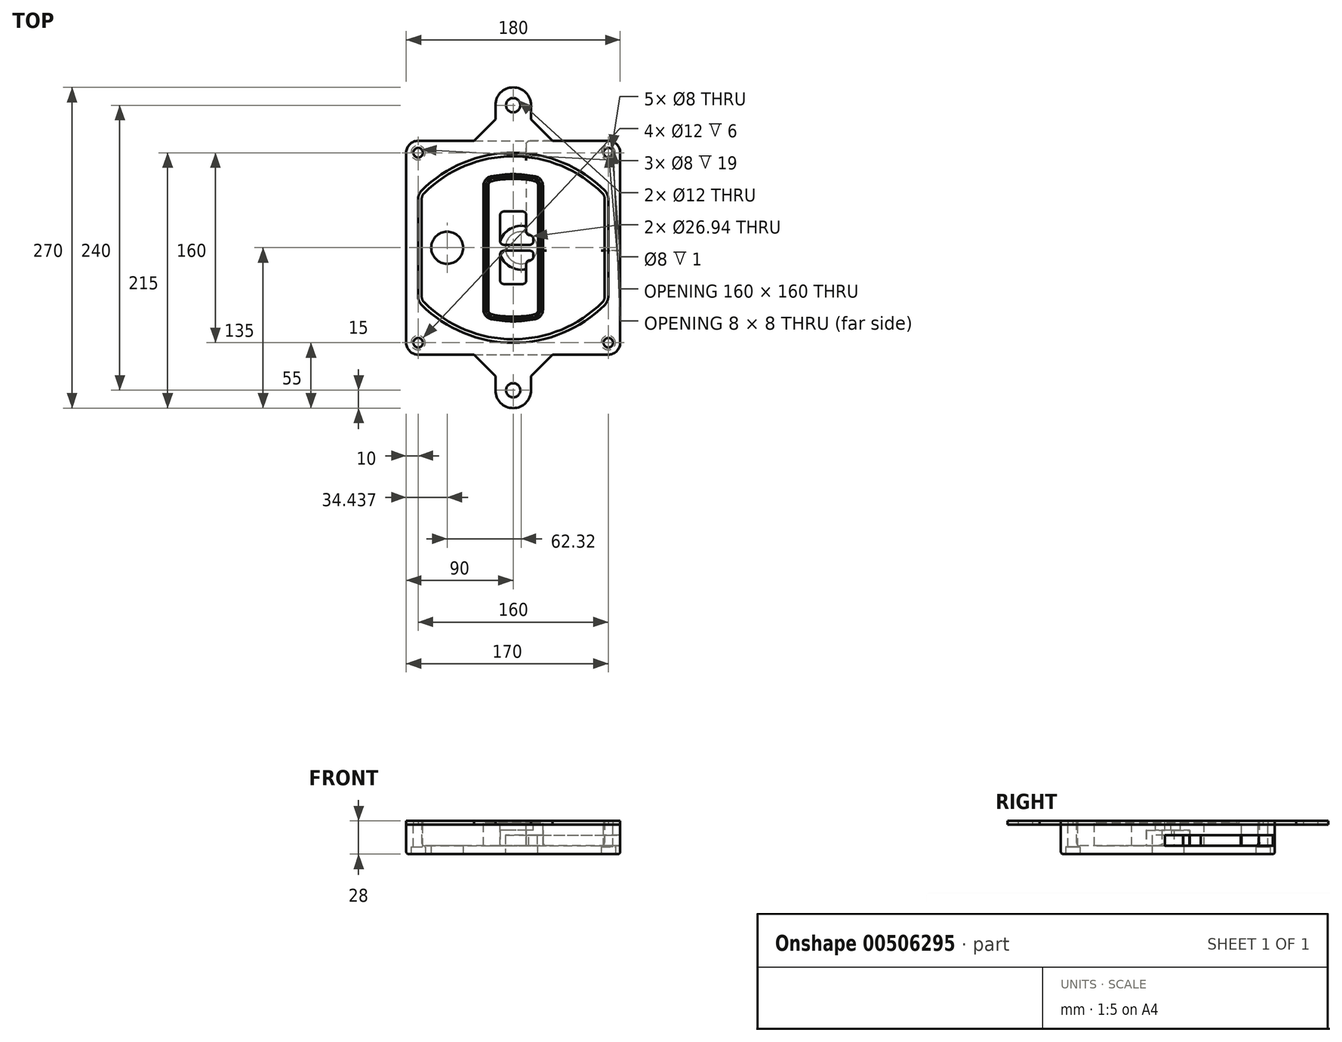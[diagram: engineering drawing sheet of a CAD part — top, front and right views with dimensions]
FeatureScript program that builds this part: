
annotation { "Feature Type Name" : "Feature", "Feature Type Description" : "" }
export const myFeature = defineFeature(function(context is Context, id is Id, definition is map)
    precondition{}
    {
        {
            var Q0;
            Q0=qCreatedBy(makeId("Top.planeOp"),FACE);
            var sketch = newSketch(context, id + "F0", { "sketchPlane" : qUnion([Q0])});
            skPoint(sketch, "E0.rect.middle", {"position": v(0, 0) * mm});
            skLineSegment(sketch, "E1.bottom", {"start": v(-80, -90) * mm, "end": v(80, -90) * mm});
            skLineSegment(sketch, "E1.top", {"start": v(-80, 90) * mm, "end": v(80, 90) * mm});
            skLineSegment(sketch, "E1.left", {"start": v(-90, -80) * mm, "end": v(-90, 80) * mm});
            skLineSegment(sketch, "E1.right", {"start": v(90, -80) * mm, "end": v(90, 80) * mm});
            skLineSegment(sketch, "E2", {"start": v(-90, 90) * mm, "end": v(90, -90) * mm, "construction": true});
            skLineSegment(sketch, "E3", {"start": v(90, 90) * mm, "end": v(-90, -90) * mm, "construction": true});
            skCircle(sketch, "E4", {"center": v(-80, 80) * mm, "radius": 4 * mm});
            skCircle(sketch, "E5", {"center": v(80, 80) * mm, "radius": 4 * mm});
            skCircle(sketch, "E6", {"center": v(80, -80) * mm, "radius": 4 * mm});
            skCircle(sketch, "E7", {"center": v(-80, -80) * mm, "radius": 4 * mm});
            skLineSegment(sketch, "E8", {"start": v(-80, 80) * mm, "end": v(80, 80) * mm, "construction": true});
            skLineSegment(sketch, "E9", {"start": v(80, 80) * mm, "end": v(80, -80) * mm, "construction": true});
            skLineSegment(sketch, "E10", {"start": v(80, -80) * mm, "end": v(-80, -80) * mm, "construction": true});
            skLineSegment(sketch, "E11", {"start": v(-80, -80) * mm, "end": v(-80, 80) * mm, "construction": true});
            skLineSegment(sketch, "E12", {"start": v(-80, 40.98) * mm, "end": v(-80, -40.98) * mm});
            skLineSegment(sketch, "E13", {"start": v(80, 40.98) * mm, "end": v(80, -40.98) * mm});
            skArc(sketch, "E14", {"start": v(77.08, 48.04) * mm, "mid": v(0, 80) * mm, "end": v(-77.08, 48.04) * mm});
            skArc(sketch, "E15", {"start": v(-77.08, -48.04) * mm, "mid": v(0, -80) * mm, "end": v(77.08, -48.04) * mm});
            skLineSegment(sketch, "E16", {"start": v(-80, 0) * mm, "end": v(80, 0) * mm, "construction": true});
            skPoint(sketch, "E17.visualSharp", {"position": v(-80, -45) * mm});
            skArc(sketch, "E17.filletArc", {"start": v(-80, -40.98) * mm, "mid": v(-79.24, -44.8) * mm, "end": v(-77.08, -48.04) * mm});
            skPoint(sketch, "E18.visualSharp", {"position": v(-80, 45) * mm});
            skArc(sketch, "E18.filletArc", {"start": v(-77.08, 48.04) * mm, "mid": v(-79.24, 44.8) * mm, "end": v(-80, 40.98) * mm});
            skPoint(sketch, "E19.visualSharp", {"position": v(80, 45) * mm});
            skArc(sketch, "E19.filletArc", {"start": v(80, 40.98) * mm, "mid": v(79.24, 44.8) * mm, "end": v(77.08, 48.04) * mm});
            skPoint(sketch, "E20.visualSharp", {"position": v(80, -45) * mm});
            skArc(sketch, "E20.filletArc", {"start": v(77.08, -48.04) * mm, "mid": v(79.24, -44.8) * mm, "end": v(80, -40.98) * mm});
            skPoint(sketch, "E21.visualSharp", {"position": v(-90, 90) * mm});
            skArc(sketch, "E21.filletArc", {"start": v(-80, 90) * mm, "mid": v(-87.07, 87.07) * mm, "end": v(-90, 80) * mm});
            skPoint(sketch, "E22.visualSharp", {"position": v(90, 90) * mm});
            skArc(sketch, "E22.filletArc", {"start": v(90, 80) * mm, "mid": v(87.07, 87.07) * mm, "end": v(80, 90) * mm});
            skPoint(sketch, "E23.visualSharp", {"position": v(90, -90) * mm});
            skArc(sketch, "E23.filletArc", {"start": v(80, -90) * mm, "mid": v(87.07, -87.07) * mm, "end": v(90, -80) * mm});
            skPoint(sketch, "E24.visualSharp", {"position": v(-90, -90) * mm});
            skArc(sketch, "E24.filletArc", {"start": v(-90, -80) * mm, "mid": v(-87.07, -87.07) * mm, "end": v(-80, -90) * mm});
            skArc(sketch, "E25.0", {"start": v(77, 40.98) * mm, "mid": v(76.47, 43.65) * mm, "end": v(74.95, 45.92) * mm});
            skLineSegment(sketch, "E25.1", {"start": v(77, 40.98) * mm, "end": v(77, -40.98) * mm});
            skArc(sketch, "E25.2", {"start": v(74.95, -45.92) * mm, "mid": v(76.47, -43.65) * mm, "end": v(77, -40.98) * mm});
            skArc(sketch, "E25.3", {"start": v(-74.95, -45.92) * mm, "mid": v(0, -77) * mm, "end": v(74.95, -45.92) * mm});
            skArc(sketch, "E25.4", {"start": v(-77, -40.98) * mm, "mid": v(-76.47, -43.65) * mm, "end": v(-74.95, -45.92) * mm});
            skArc(sketch, "E25.5", {"start": v(74.95, 45.92) * mm, "mid": v(0, 77) * mm, "end": v(-74.95, 45.92) * mm});
            skLineSegment(sketch, "E25.6", {"start": v(-77, 40.98) * mm, "end": v(-77, -40.98) * mm});
            skArc(sketch, "E25.7", {"start": v(-74.95, 45.92) * mm, "mid": v(-76.47, 43.65) * mm, "end": v(-77, 40.98) * mm});
            skArc(sketch, "E26.0", {"start": v(-79.9, 50.87) * mm, "mid": v(-82.94, 46.33) * mm, "end": v(-84, 40.98) * mm});
            skArc(sketch, "E26.1", {"start": v(79.9, 50.87) * mm, "mid": v(0, 84) * mm, "end": v(-79.9, 50.87) * mm});
            skArc(sketch, "E26.2", {"start": v(84, 40.98) * mm, "mid": v(82.94, 46.33) * mm, "end": v(79.9, 50.87) * mm});
            skLineSegment(sketch, "E26.3", {"start": v(84, 40.98) * mm, "end": v(84, -40.98) * mm});
            skArc(sketch, "E26.4", {"start": v(79.9, -50.87) * mm, "mid": v(82.94, -46.33) * mm, "end": v(84, -40.98) * mm});
            skLineSegment(sketch, "E26.5", {"start": v(-84, 40.98) * mm, "end": v(-84, -40.98) * mm});
            skArc(sketch, "E26.6", {"start": v(-79.9, -50.87) * mm, "mid": v(0, -84) * mm, "end": v(79.9, -50.87) * mm});
            skArc(sketch, "E26.7", {"start": v(-84, -40.98) * mm, "mid": v(-82.94, -46.33) * mm, "end": v(-79.9, -50.87) * mm});
            skSolve(sketch);
        }
        {
            var Q0;
            Q0=makeQuery(id+"F0.imprint","IMPRINT",FACE,{"disambiguationData":[TD([[makeQuery(id+"F0.imprint","IMPRINT",EDGE,{"derivedFrom":sQuery(id+"F0.wireOp",EDGE,"E1.bottom")}),1.0]])]});
            var Q1;
            Q1=makeQuery(id+"F0.imprint","IMPRINT",FACE,{"disambiguationData":[TD([[makeQuery(id+"F0.imprint","IMPRINT",EDGE,{"derivedFrom":sQuery(id+"F0.wireOp",EDGE,"E12")}),1.0]])]});
            var Q2;
            Q2=makeQuery(id+"F0.imprint","IMPRINT",FACE,{"disambiguationData":[TD([[makeQuery(id+"F0.imprint","IMPRINT",EDGE,{"derivedFrom":sQuery(id+"F0.wireOp",EDGE,"E25.0")}),1.0]])]});
            var Q3;
            Q3=makeQuery(id+"F0.imprint","IMPRINT",FACE,{"disambiguationData":[TD([[makeQuery(id+"F0.imprint","IMPRINT",EDGE,{"derivedFrom":sQuery(id+"F0.wireOp",EDGE,"E12")}),-1.0]])]});
            extrude(context, id + "F1", {"entities" : qUnion([Q0, Q1, Q2, Q3]), "oppositeDirection" : true, "depth" : 25 * mm});
        }
        {
            var Q0;
            Q0=makeQuery(id+"F0.imprint","IMPRINT",FACE,{"disambiguationData":[TD([[makeQuery(id+"F0.imprint","IMPRINT",EDGE,{"derivedFrom":sQuery(id+"F0.wireOp",EDGE,"E12")}),1.0]])]});
            extrude(context, id + "F2", {"entities" : qUnion([Q0]), "operationType" : NewBodyOperationType.ADD, "depth" : 3 * mm});
        }
        {
            var Q0;
            Q0=makeQuery(id+"F0.imprint","IMPRINT",FACE,{"disambiguationData":[TD([[makeQuery(id+"F0.imprint","IMPRINT",EDGE,{"derivedFrom":sQuery(id+"F0.wireOp",EDGE,"E25.0")}),1.0]])]});
            extrude(context, id + "F3", {"entities" : qUnion([Q0]), "operationType" : NewBodyOperationType.REMOVE, "oppositeDirection" : true, "depth" : 18 * mm});
        }
        {
            var Q0;
            Q0=makeQuery(id+"F2.opExtrude","CAP_FACE",FACE,{"disambiguationData":[OSD([sQuery(id+"F0.wireOp",EDGE,"E12"),sQuery(id+"F0.wireOp",EDGE,"E13"),sQuery(id+"F0.wireOp",EDGE,"E14"),sQuery(id+"F0.wireOp",EDGE,"E15"),sQuery(id+"F0.wireOp",EDGE,"E17.filletArc"),sQuery(id+"F0.wireOp",EDGE,"E18.filletArc"),sQuery(id+"F0.wireOp",EDGE,"E19.filletArc"),sQuery(id+"F0.wireOp",EDGE,"E20.filletArc"),sQuery(id+"F0.wireOp",EDGE,"E25.0"),sQuery(id+"F0.wireOp",EDGE,"E25.1"),sQuery(id+"F0.wireOp",EDGE,"E25.2"),sQuery(id+"F0.wireOp",EDGE,"E25.3"),sQuery(id+"F0.wireOp",EDGE,"E25.4"),sQuery(id+"F0.wireOp",EDGE,"E25.5"),sQuery(id+"F0.wireOp",EDGE,"E25.6"),sQuery(id+"F0.wireOp",EDGE,"E25.7")])],"isStart":false});
            var sketch = newSketch(context, id + "F4", { "sketchPlane" : qUnion([Q0])});
            skArc(sketch, "E27.0", {"start": v(-18.64, -60.07) * mm, "mid": v(0, -62) * mm, "end": v(18.64, -60.07) * mm});
            skArc(sketch, "E28.0", {"start": v(18.64, 60.07) * mm, "mid": v(0, 62) * mm, "end": v(-18.64, 60.07) * mm});
            skLineSegment(sketch, "E29", {"start": v(-25, 52.24) * mm, "end": v(-25, -52.24) * mm});
            skLineSegment(sketch, "E30", {"start": v(25, 52.24) * mm, "end": v(25, -52.24) * mm});
            skLineSegment(sketch, "E31", {"start": v(-25, 58.5) * mm, "end": v(25, 58.5) * mm, "construction": true});
            skLineSegment(sketch, "E32", {"start": v(-25, -58.5) * mm, "end": v(25, -58.5) * mm, "construction": true});
            skPoint(sketch, "E33.visualSharp", {"position": v(-25, 58.5) * mm});
            skArc(sketch, "E33.filletArc", {"start": v(-18.64, 60.07) * mm, "mid": v(-23.2, 57.28) * mm, "end": v(-25, 52.24) * mm});
            skPoint(sketch, "E34.visualSharp", {"position": v(25, 58.5) * mm});
            skArc(sketch, "E34.filletArc", {"start": v(25, 52.24) * mm, "mid": v(23.2, 57.28) * mm, "end": v(18.64, 60.07) * mm});
            skPoint(sketch, "E35.visualSharp", {"position": v(25, -58.5) * mm});
            skArc(sketch, "E35.filletArc", {"start": v(18.64, -60.07) * mm, "mid": v(23.2, -57.28) * mm, "end": v(25, -52.24) * mm});
            skPoint(sketch, "E36.visualSharp", {"position": v(-25, -58.5) * mm});
            skArc(sketch, "E36.filletArc", {"start": v(-25, -52.24) * mm, "mid": v(-23.2, -57.28) * mm, "end": v(-18.64, -60.07) * mm});
            skArc(sketch, "E37.0", {"start": v(74.95, 45.92) * mm, "mid": v(0, 77) * mm, "end": v(-74.95, 45.92) * mm});
            skArc(sketch, "E37.1", {"start": v(-74.95, 45.92) * mm, "mid": v(-76.47, 43.65) * mm, "end": v(-77, 40.98) * mm});
            skLineSegment(sketch, "E37.2", {"start": v(-77, 40.98) * mm, "end": v(-77, -40.98) * mm});
            skArc(sketch, "E37.3", {"start": v(-77, -40.98) * mm, "mid": v(-76.47, -43.65) * mm, "end": v(-74.95, -45.92) * mm});
            skArc(sketch, "E37.4", {"start": v(-74.95, -45.92) * mm, "mid": v(0, -77) * mm, "end": v(74.95, -45.92) * mm});
            skArc(sketch, "E37.5", {"start": v(74.95, -45.92) * mm, "mid": v(76.47, -43.65) * mm, "end": v(77, -40.98) * mm});
            skLineSegment(sketch, "E37.6", {"start": v(77, 40.98) * mm, "end": v(77, -40.98) * mm});
            skArc(sketch, "E37.7", {"start": v(77, 40.98) * mm, "mid": v(76.47, 43.65) * mm, "end": v(74.95, 45.92) * mm});
            skLineSegment(sketch, "E38.0", {"start": v(23, 52.24) * mm, "end": v(23, -52.24) * mm});
            skArc(sketch, "E38.1", {"start": v(18.23, -58.11) * mm, "mid": v(21.66, -56.02) * mm, "end": v(23, -52.24) * mm});
            skArc(sketch, "E38.2", {"start": v(-18.23, -58.11) * mm, "mid": v(0, -60) * mm, "end": v(18.23, -58.11) * mm});
            skArc(sketch, "E38.3", {"start": v(-23, -52.24) * mm, "mid": v(-21.66, -56.02) * mm, "end": v(-18.23, -58.11) * mm});
            skLineSegment(sketch, "E38.4", {"start": v(-23, 52.24) * mm, "end": v(-23, -52.24) * mm});
            skArc(sketch, "E38.5", {"start": v(23, 52.24) * mm, "mid": v(21.66, 56.02) * mm, "end": v(18.23, 58.11) * mm});
            skArc(sketch, "E38.6", {"start": v(-18.23, 58.11) * mm, "mid": v(-21.66, 56.02) * mm, "end": v(-23, 52.24) * mm});
            skArc(sketch, "E38.7", {"start": v(18.23, 58.11) * mm, "mid": v(0, 60) * mm, "end": v(-18.23, 58.11) * mm});
            skArc(sketch, "E39.0", {"start": v(21, 52.24) * mm, "mid": v(20.1, 54.76) * mm, "end": v(17.82, 56.15) * mm});
            skLineSegment(sketch, "E39.1", {"start": v(21, 52.24) * mm, "end": v(21, -52.24) * mm});
            skArc(sketch, "E39.2", {"start": v(17.82, -56.15) * mm, "mid": v(20.1, -54.76) * mm, "end": v(21, -52.24) * mm});
            skArc(sketch, "E39.3", {"start": v(-17.82, -56.15) * mm, "mid": v(0, -58) * mm, "end": v(17.82, -56.15) * mm});
            skArc(sketch, "E39.4", {"start": v(-21, -52.24) * mm, "mid": v(-20.1, -54.76) * mm, "end": v(-17.82, -56.15) * mm});
            skArc(sketch, "E39.5", {"start": v(17.82, 56.15) * mm, "mid": v(0, 58) * mm, "end": v(-17.82, 56.15) * mm});
            skLineSegment(sketch, "E39.6", {"start": v(-21, 52.24) * mm, "end": v(-21, -52.24) * mm});
            skArc(sketch, "E39.7", {"start": v(-17.82, 56.15) * mm, "mid": v(-20.1, 54.76) * mm, "end": v(-21, 52.24) * mm});
            skLineSegment(sketch, "E40", {"start": v(-25, 0) * mm, "end": v(25, 0) * mm, "construction": true});
            skLineSegment(sketch, "E41", {"start": v(-11, 5.5) * mm, "end": v(-11, 27.5) * mm});
            skLineSegment(sketch, "E42", {"start": v(-8, 30.5) * mm, "end": v(8, 30.5) * mm});
            skLineSegment(sketch, "E43", {"start": v(11, 27.5) * mm, "end": v(11, 13.5) * mm});
            skLineSegment(sketch, "E44", {"start": v(14, 10.5) * mm, "end": v(14, 10.5) * mm});
            skLineSegment(sketch, "E45", {"start": v(17, 7.5) * mm, "end": v(17, 5.5) * mm});
            skLineSegment(sketch, "E46", {"start": v(14, 2.5) * mm, "end": v(-8, 2.5) * mm});
            skPoint(sketch, "E47.visualSharp", {"position": v(-11, 30.5) * mm});
            skArc(sketch, "E47.filletArc", {"start": v(-8, 30.5) * mm, "mid": v(-10.12, 29.62) * mm, "end": v(-11, 27.5) * mm});
            skPoint(sketch, "E48.visualSharp", {"position": v(11, 30.5) * mm});
            skArc(sketch, "E48.filletArc", {"start": v(11, 27.5) * mm, "mid": v(10.12, 29.62) * mm, "end": v(8, 30.5) * mm});
            skPoint(sketch, "E49.visualSharp", {"position": v(11, 10.5) * mm});
            skArc(sketch, "E49.filletArc", {"start": v(11, 13.5) * mm, "mid": v(11.88, 11.38) * mm, "end": v(14, 10.5) * mm});
            skPoint(sketch, "E50.visualSharp", {"position": v(17, 10.5) * mm});
            skArc(sketch, "E50.filletArc", {"start": v(17, 7.5) * mm, "mid": v(16.12, 9.62) * mm, "end": v(14, 10.5) * mm});
            skPoint(sketch, "E51.visualSharp", {"position": v(17, 2.5) * mm});
            skArc(sketch, "E51.filletArc", {"start": v(14, 2.5) * mm, "mid": v(16.12, 3.38) * mm, "end": v(17, 5.5) * mm});
            skPoint(sketch, "E52.visualSharp", {"position": v(-11, 2.5) * mm});
            skArc(sketch, "E52.filletArc", {"start": v(-11, 5.5) * mm, "mid": v(-10.12, 3.38) * mm, "end": v(-8, 2.5) * mm});
            skLineSegment(sketch, "E53.0.MirrorCS", {"start": v(14, -2.5) * mm, "end": v(-8, -2.5) * mm});
            skArc(sketch, "E54.0.MirrorCS", {"start": v(-11, -5.5) * mm, "mid": v(-10.12, -3.38) * mm, "end": v(-8, -2.5) * mm});
            skLineSegment(sketch, "E55.0.MirrorCS", {"start": v(-11, -5.5) * mm, "end": v(-11, -27.5) * mm});
            skArc(sketch, "E56.0.MirrorCS", {"start": v(-8, -30.5) * mm, "mid": v(-10.12, -29.62) * mm, "end": v(-11, -27.5) * mm});
            skLineSegment(sketch, "E57.0.MirrorCS", {"start": v(-8, -30.5) * mm, "end": v(8, -30.5) * mm});
            skArc(sketch, "E58.0.MirrorCS", {"start": v(11, -27.5) * mm, "mid": v(10.12, -29.62) * mm, "end": v(8, -30.5) * mm});
            skLineSegment(sketch, "E59.0.MirrorCS", {"start": v(11, -27.5) * mm, "end": v(11, -13.5) * mm});
            skArc(sketch, "E60.0.MirrorCS", {"start": v(11, -13.5) * mm, "mid": v(11.88, -11.38) * mm, "end": v(14, -10.5) * mm});
            skArc(sketch, "E61.0.MirrorCS", {"start": v(17, -7.5) * mm, "mid": v(16.12, -9.62) * mm, "end": v(14, -10.5) * mm});
            skLineSegment(sketch, "E62.0.MirrorCS", {"start": v(17, -7.5) * mm, "end": v(17, -5.5) * mm});
            skArc(sketch, "E63.0.MirrorCS", {"start": v(14, -2.5) * mm, "mid": v(16.12, -3.38) * mm, "end": v(17, -5.5) * mm});
            skSolve(sketch);
        }
        {
            var Q0;
            Q0=makeQuery(id+"F4.imprint","IMPRINT",FACE,{"disambiguationData":[TD([[makeQuery(id+"F4.imprint","IMPRINT",EDGE,{"derivedFrom":sQuery(id+"F4.wireOp",EDGE,"E27.0")}),1.0]])]});
            var Q1;
            Q1=makeQuery(id+"F4.imprint","IMPRINT",FACE,{"disambiguationData":[TD([[makeQuery(id+"F4.imprint","IMPRINT",EDGE,{"derivedFrom":sQuery(id+"F4.wireOp",EDGE,"E38.0")}),-1.0]])]});
            var Q2;
            Q2=makeQuery(id+"F4.imprint","IMPRINT",FACE,{"disambiguationData":[TD([[makeQuery(id+"F4.imprint","IMPRINT",EDGE,{"derivedFrom":sQuery(id+"F4.wireOp",EDGE,"E39.0")}),1.0]])]});
            extrude(context, id + "F5", {"entities" : qUnion([Q0, Q1, Q2]), "operationType" : NewBodyOperationType.ADD, "endBound" : BoundingType.UP_TO_NEXT, "oppositeDirection" : true, "depth" : 25 * mm});
        }
        {
            var Q0;
            Q0=makeQuery(id+"F4.imprint","IMPRINT",FACE,{"disambiguationData":[TD([[makeQuery(id+"F4.imprint","IMPRINT",EDGE,{"derivedFrom":sQuery(id+"F4.wireOp",EDGE,"E38.0")}),-1.0]])]});
            extrude(context, id + "F6", {"entities" : qUnion([Q0]), "operationType" : NewBodyOperationType.REMOVE, "oppositeDirection" : true, "depth" : 2 * mm});
        }
        {
            var Q0;
            Q0=makeQuery(id+"F1.opExtrude","CAP_FACE",FACE,{"disambiguationData":[OSD([sQuery(id+"F0.wireOp",EDGE,"E1.bottom"),sQuery(id+"F0.wireOp",EDGE,"E1.top"),sQuery(id+"F0.wireOp",EDGE,"E1.left"),sQuery(id+"F0.wireOp",EDGE,"E1.right"),sQuery(id+"F0.wireOp",EDGE,"E4"),sQuery(id+"F0.wireOp",EDGE,"E5"),sQuery(id+"F0.wireOp",EDGE,"E6"),sQuery(id+"F0.wireOp",EDGE,"E7"),sQuery(id+"F0.wireOp",EDGE,"E21.filletArc"),sQuery(id+"F0.wireOp",EDGE,"E22.filletArc"),sQuery(id+"F0.wireOp",EDGE,"E23.filletArc"),sQuery(id+"F0.wireOp",EDGE,"E24.filletArc")])],"isStart":false});
            var sketch = newSketch(context, id + "F7", { "sketchPlane" : qUnion([Q0])});
            skCircle(sketch, "E64", {"center": v(6.76, 0) * mm, "radius": 13.47 * mm});
            skCircle(sketch, "E65", {"center": v(-55.56, 0) * mm, "radius": 13.47 * mm});
            skLineSegment(sketch, "E66", {"start": v(90, 0) * mm, "end": v(-90, 0) * mm});
            skCircle(sketch, "E67", {"center": v(6.76, 0) * mm, "radius": 18.47 * mm});
            skCircle(sketch, "E68", {"center": v(80, -80) * mm, "radius": 6 * mm});
            skCircle(sketch, "E69", {"center": v(-80, -80) * mm, "radius": 6 * mm});
            skCircle(sketch, "E70", {"center": v(-80, 80) * mm, "radius": 6 * mm});
            skCircle(sketch, "E71", {"center": v(80, 80) * mm, "radius": 6 * mm});
            skSolve(sketch);
        }
        {
            var Q0;
            {var subQ1=sQuery(id+"F7.wireOp",EDGE,"E66");var subQ4=sQuery(id+"F7.wireOp",EDGE,"E64");var subQ6=makeQuery(id+"F7.imprint","INTERSECT",VERTEX,{"disambiguationData":[OD(0.0)],"derivedFrom":[subQ4,subQ1]});Q0=makeQuery(id+"F7.imprint","IMPRINT",FACE,{"disambiguationData":[TD([[makeQuery(id+"F7.imprint","IMPRINT",EDGE,{"disambiguationData":[TD([[subQ6,-1.0]])],"derivedFrom":subQ4}),-1.0]])]});}
            var Q1;
            {var subQ0=sQuery(id+"F7.wireOp",EDGE,"E66");var subQ1=sQuery(id+"F7.wireOp",EDGE,"E64");var subQ3=makeQuery(id+"F7.imprint","INTERSECT",VERTEX,{"disambiguationData":[OD(0.0)],"derivedFrom":[subQ1,subQ0]});Q1=makeQuery(id+"F7.imprint","IMPRINT",FACE,{"disambiguationData":[TD([[makeQuery(id+"F7.imprint","IMPRINT",EDGE,{"disambiguationData":[TD([[subQ3,-1.0]])],"derivedFrom":subQ1}),1.0]])]});}
            var Q2;
            {var subQ0=sQuery(id+"F7.wireOp",EDGE,"E66");var subQ1=sQuery(id+"F7.wireOp",EDGE,"E64");var subQ3=makeQuery(id+"F7.imprint","INTERSECT",VERTEX,{"disambiguationData":[OD(0.0)],"derivedFrom":[subQ1,subQ0]});Q2=makeQuery(id+"F7.imprint","IMPRINT",FACE,{"disambiguationData":[TD([[makeQuery(id+"F7.imprint","IMPRINT",EDGE,{"disambiguationData":[TD([[subQ3,1.0]])],"derivedFrom":subQ1}),1.0]])]});}
            var Q3;
            {var subQ1=sQuery(id+"F7.wireOp",EDGE,"E66");var subQ4=sQuery(id+"F7.wireOp",EDGE,"E64");var subQ6=makeQuery(id+"F7.imprint","INTERSECT",VERTEX,{"disambiguationData":[OD(0.0)],"derivedFrom":[subQ4,subQ1]});Q3=makeQuery(id+"F7.imprint","IMPRINT",FACE,{"disambiguationData":[TD([[makeQuery(id+"F7.imprint","IMPRINT",EDGE,{"disambiguationData":[TD([[subQ6,1.0]])],"derivedFrom":subQ4}),-1.0]])]});}
            extrude(context, id + "F8", {"entities" : qUnion([Q0, Q1, Q2, Q3]), "operationType" : NewBodyOperationType.ADD, "oppositeDirection" : true, "depth" : 20 * mm});
        }
        {
            var Q0;
            {var subQ0=sQuery(id+"F7.wireOp",EDGE,"E66");var subQ1=sQuery(id+"F7.wireOp",EDGE,"E64");var subQ3=makeQuery(id+"F7.imprint","INTERSECT",VERTEX,{"disambiguationData":[OD(0.0)],"derivedFrom":[subQ1,subQ0]});Q0=makeQuery(id+"F7.imprint","IMPRINT",FACE,{"disambiguationData":[TD([[makeQuery(id+"F7.imprint","IMPRINT",EDGE,{"disambiguationData":[TD([[subQ3,-1.0]])],"derivedFrom":subQ1}),1.0]])]});}
            var Q1;
            {var subQ0=sQuery(id+"F7.wireOp",EDGE,"E66");var subQ1=sQuery(id+"F7.wireOp",EDGE,"E64");var subQ3=makeQuery(id+"F7.imprint","INTERSECT",VERTEX,{"disambiguationData":[OD(0.0)],"derivedFrom":[subQ1,subQ0]});Q1=makeQuery(id+"F7.imprint","IMPRINT",FACE,{"disambiguationData":[TD([[makeQuery(id+"F7.imprint","IMPRINT",EDGE,{"disambiguationData":[TD([[subQ3,1.0]])],"derivedFrom":subQ1}),1.0]])]});}
            extrude(context, id + "F9", {"entities" : qUnion([Q0, Q1]), "operationType" : NewBodyOperationType.REMOVE, "oppositeDirection" : true, "depth" : 16 * mm});
        }
        {
            var Q0;
            {var subQ0=sQuery(id+"F7.wireOp",EDGE,"E66");var subQ1=sQuery(id+"F7.wireOp",EDGE,"E65");var subQ3=makeQuery(id+"F7.imprint","INTERSECT",VERTEX,{"disambiguationData":[OD(0.0)],"derivedFrom":[subQ1,subQ0]});Q0=makeQuery(id+"F7.imprint","IMPRINT",FACE,{"disambiguationData":[TD([[makeQuery(id+"F7.imprint","IMPRINT",EDGE,{"disambiguationData":[TD([[subQ3,-1.0]])],"derivedFrom":subQ1}),1.0]])]});}
            var Q1;
            {var subQ0=sQuery(id+"F7.wireOp",EDGE,"E66");var subQ1=sQuery(id+"F7.wireOp",EDGE,"E65");var subQ3=makeQuery(id+"F7.imprint","INTERSECT",VERTEX,{"disambiguationData":[OD(0.0)],"derivedFrom":[subQ1,subQ0]});Q1=makeQuery(id+"F7.imprint","IMPRINT",FACE,{"disambiguationData":[TD([[makeQuery(id+"F7.imprint","IMPRINT",EDGE,{"disambiguationData":[TD([[subQ3,1.0]])],"derivedFrom":subQ1}),1.0]])]});}
            extrude(context, id + "F10", {"entities" : qUnion([Q0, Q1]), "operationType" : NewBodyOperationType.REMOVE, "oppositeDirection" : true, "depth" : 25 * mm});
        }
        {
            var Q0;
            Q0=makeQuery(id+"F7.imprint","IMPRINT",FACE,{"disambiguationData":[TD([[makeQuery(id+"F7.imprint","IMPRINT",EDGE,{"derivedFrom":sQuery(id+"F7.wireOp",EDGE,"E68")}),1.0]])]});
            var Q1;
            Q1=makeQuery(id+"F7.imprint","IMPRINT",FACE,{"disambiguationData":[TD([[makeQuery(id+"F7.imprint","IMPRINT",EDGE,{"derivedFrom":makeQuery(id+"F1.opExtrude","CAP_EDGE",EDGE,{"disambiguationData":[OSD([sQuery(id+"F0.wireOp",EDGE,"E5")])],"isStart":false})}),-1.0]])]});
            var Q2;
            Q2=makeQuery(id+"F7.imprint","IMPRINT",FACE,{"disambiguationData":[TD([[makeQuery(id+"F7.imprint","IMPRINT",EDGE,{"derivedFrom":sQuery(id+"F7.wireOp",EDGE,"E69")}),1.0]])]});
            var Q3;
            Q3=makeQuery(id+"F7.imprint","IMPRINT",FACE,{"disambiguationData":[TD([[makeQuery(id+"F7.imprint","IMPRINT",EDGE,{"derivedFrom":makeQuery(id+"F1.opExtrude","CAP_EDGE",EDGE,{"disambiguationData":[OSD([sQuery(id+"F0.wireOp",EDGE,"E4")])],"isStart":false})}),-1.0]])]});
            var Q4;
            Q4=makeQuery(id+"F7.imprint","IMPRINT",FACE,{"disambiguationData":[TD([[makeQuery(id+"F7.imprint","IMPRINT",EDGE,{"derivedFrom":sQuery(id+"F7.wireOp",EDGE,"E70")}),1.0]])]});
            var Q5;
            Q5=makeQuery(id+"F7.imprint","IMPRINT",FACE,{"disambiguationData":[TD([[makeQuery(id+"F7.imprint","IMPRINT",EDGE,{"derivedFrom":makeQuery(id+"F1.opExtrude","CAP_EDGE",EDGE,{"disambiguationData":[OSD([sQuery(id+"F0.wireOp",EDGE,"E7")])],"isStart":false})}),-1.0]])]});
            var Q6;
            Q6=makeQuery(id+"F7.imprint","IMPRINT",FACE,{"disambiguationData":[TD([[makeQuery(id+"F7.imprint","IMPRINT",EDGE,{"derivedFrom":sQuery(id+"F7.wireOp",EDGE,"E71")}),1.0]])]});
            var Q7;
            Q7=makeQuery(id+"F7.imprint","IMPRINT",FACE,{"disambiguationData":[TD([[makeQuery(id+"F7.imprint","IMPRINT",EDGE,{"derivedFrom":makeQuery(id+"F1.opExtrude","CAP_EDGE",EDGE,{"disambiguationData":[OSD([sQuery(id+"F0.wireOp",EDGE,"E6")])],"isStart":false})}),-1.0]])]});
            extrude(context, id + "F11", {"entities" : qUnion([Q0, Q1, Q2, Q3, Q4, Q5, Q6, Q7]), "operationType" : NewBodyOperationType.REMOVE, "oppositeDirection" : true, "depth" : 6 * mm});
        }
        {
            var Q0;
            Q0=makeQuery(id+"F9.boolean.opBoolean","COPY",FACE,{"derivedFrom":makeQuery(id+"F9.opExtrude","CAP_FACE",FACE,{"disambiguationData":[OSD([sQuery(id+"F7.wireOp",EDGE,"E64")])],"isStart":false})});
            var sketch = newSketch(context, id + "F12", { "sketchPlane" : qUnion([Q0])});
            skArc(sketch, "E72.0", {"start": v(11, -88.19) * mm, "mid": v(97.1, -83.6) * mm, "end": v(92.5, 2.5) * mm});
            skLineSegment(sketch, "E72.1", {"start": v(11, -17.97) * mm, "end": v(11, -17.97) * mm});
            skLineSegment(sketch, "E73", {"start": v(92.5, -105.13) * mm, "end": v(102.3, -105.13) * mm});
            skLineSegment(sketch, "E74.0", {"start": v(92.5, 2.5) * mm, "end": v(14, 2.5) * mm});
            skArc(sketch, "E74.1", {"start": v(14, 2.5) * mm, "mid": v(16.12, 3.38) * mm, "end": v(17, 5.5) * mm});
            skLineSegment(sketch, "E74.2", {"start": v(17, 7.5) * mm, "end": v(17, 5.5) * mm});
            skArc(sketch, "E74.3", {"start": v(17, 7.5) * mm, "mid": v(16.12, 9.62) * mm, "end": v(14, 10.5) * mm});
            skArc(sketch, "E74.4", {"start": v(11, 13.5) * mm, "mid": v(11.88, 11.38) * mm, "end": v(14, 10.5) * mm});
            skLineSegment(sketch, "E74.5", {"start": v(11, 13.5) * mm, "end": v(11, -88.19) * mm});
            skLineSegment(sketch, "E74.7", {"start": v(92.5, -2.5) * mm, "end": v(14, -2.5) * mm});
            skArc(sketch, "E74.8", {"start": v(14, -2.5) * mm, "mid": v(16.12, -3.38) * mm, "end": v(17, -5.5) * mm});
            skLineSegment(sketch, "E74.9", {"start": v(17, -7.5) * mm, "end": v(17, -5.5) * mm});
            skArc(sketch, "E74.10", {"start": v(17, -7.5) * mm, "mid": v(16.12, -9.62) * mm, "end": v(14, -10.5) * mm});
            skArc(sketch, "E74.11", {"start": v(11, -13.5) * mm, "mid": v(11.88, -11.38) * mm, "end": v(14, -10.5) * mm});
            skLineSegment(sketch, "E74.12", {"start": v(11, -17.97) * mm, "end": v(11, -13.5) * mm});
            skPoint(sketch, "E75.orphan", {"position": v(11, -27.5) * mm});
            skPoint(sketch, "E76.orphan", {"position": v(-8, -2.5) * mm});
            skPoint(sketch, "E77.orphan", {"position": v(-8, 2.5) * mm});
            skPoint(sketch, "E78.orphan", {"position": v(11, 27.5) * mm});
            skSolve(sketch);
        }
        {
            var Q0;
            {var subQ7=sQuery(id+"F12.wireOp",EDGE,"E72.0");var subQ14=sQuery(id+"F12.wireOp",EDGE,"E72.1");var subQ16=sQuery(id+"F12.wireOp",EDGE,"E74.1");var subQ18=sQuery(id+"F12.wireOp",EDGE,"E74.8");Q0=qUnion([makeQuery(id+"F12.imprint","IMPRINT",FACE,{"disambiguationData":[TD([[makeQuery(id+"F12.imprint","IMPRINT",EDGE,{"derivedFrom":subQ7}),1.0]])]}),makeQuery(id+"F12.imprint","IMPRINT",FACE,{"disambiguationData":[TD([[makeQuery(id+"F12.imprint","IMPRINT",EDGE,{"derivedFrom":subQ14}),1.0]])]}),makeQuery(id+"F12.imprint","IMPRINT",FACE,{"disambiguationData":[TD([[makeQuery(id+"F12.imprint","IMPRINT",EDGE,{"derivedFrom":subQ16}),1.0]])]}),makeQuery(id+"F12.imprint","IMPRINT",FACE,{"disambiguationData":[TD([[makeQuery(id+"F12.imprint","IMPRINT",EDGE,{"derivedFrom":subQ18}),-1.0]])]})]);}
            var Q1;
            Q1=makeQuery(id+"F5.boolean.opBoolean","SPLIT",FACE,{"disambiguationData":[TD([makeQuery(id+"F5.opExtrude","SWEPT_FACE",FACE,{"disambiguationData":[OSD([sQuery(id+"F4.wireOp",EDGE,"E41")])]})])],"derivedFrom":makeQuery(id+"F3.boolean.opBoolean","COPY",FACE,{"derivedFrom":makeQuery(id+"F3.opExtrude","CAP_FACE",FACE,{"disambiguationData":[OSD([sQuery(id+"F0.wireOp",EDGE,"E25.0"),sQuery(id+"F0.wireOp",EDGE,"E25.1"),sQuery(id+"F0.wireOp",EDGE,"E25.2"),sQuery(id+"F0.wireOp",EDGE,"E25.3"),sQuery(id+"F0.wireOp",EDGE,"E25.4"),sQuery(id+"F0.wireOp",EDGE,"E25.5"),sQuery(id+"F0.wireOp",EDGE,"E25.6"),sQuery(id+"F0.wireOp",EDGE,"E25.7")])],"isStart":false})})});
            extrude(context, id + "F13", {"entities" : qUnion([Q0]), "operationType" : NewBodyOperationType.REMOVE, "endBound" : BoundingType.UP_TO_SURFACE, "endBoundEntityFace" : qUnion([Q1]), "depth" : 25 * mm});
        }
        {
            var Q0;
            Q0=makeQuery(id+"F3.boolean.opBoolean","COPY",EDGE,{"derivedFrom":makeQuery(id+"F3.opExtrude","CAP_EDGE",EDGE,{"disambiguationData":[OSD([sQuery(id+"F0.wireOp",EDGE,"E25.6")])],"isStart":false})});
            var Q1;
            Q1=makeQuery(id+"F8.boolean.opBoolean","INTERSECT",EDGE,{"derivedFrom":[makeQuery(id+"F5.opExtrude","SWEPT_FACE",FACE,{"disambiguationData":[OSD([sQuery(id+"F4.wireOp",EDGE,"E30")])]}),makeQuery(id+"F8.opExtrude","CAP_FACE",FACE,{"disambiguationData":[OSD([sQuery(id+"F7.wireOp",EDGE,"E67")])],"isStart":false})]});
            var Q2;
            Q2=makeQuery(id+"F8.boolean.opBoolean","INTERSECT",EDGE,{"disambiguationData":[OD(1.0)],"derivedFrom":[makeQuery(id+"F5.opExtrude","SWEPT_FACE",FACE,{"disambiguationData":[OSD([sQuery(id+"F4.wireOp",EDGE,"E30")])]}),makeQuery(id+"F8.opExtrude","SWEPT_FACE",FACE,{"disambiguationData":[OSD([sQuery(id+"F7.wireOp",EDGE,"E67")])]})]});
            var Q3;
            {var subQ0=makeQuery(id+"F3.boolean.opBoolean","COPY",FACE,{"derivedFrom":makeQuery(id+"F3.opExtrude","CAP_FACE",FACE,{"disambiguationData":[OSD([sQuery(id+"F0.wireOp",EDGE,"E25.0"),sQuery(id+"F0.wireOp",EDGE,"E25.1"),sQuery(id+"F0.wireOp",EDGE,"E25.2"),sQuery(id+"F0.wireOp",EDGE,"E25.3"),sQuery(id+"F0.wireOp",EDGE,"E25.4"),sQuery(id+"F0.wireOp",EDGE,"E25.5"),sQuery(id+"F0.wireOp",EDGE,"E25.6"),sQuery(id+"F0.wireOp",EDGE,"E25.7")])],"isStart":false})});var subQ1=sQuery(id+"F4.wireOp",EDGE,"E30");Q3=makeQuery(id+"F8.boolean.opBoolean","SPLIT",EDGE,{"disambiguationData":[TD([makeQuery(id+"F5.opExtrude","SWEPT_FACE",FACE,{"disambiguationData":[OSD([sQuery(id+"F4.wireOp",EDGE,"E35.filletArc")])]})])],"derivedFrom":makeQuery(id+"F5.opExtrude","TWEAK_EDGE",EDGE,{"derivedFrom":[subQ0,makeQuery(id+"F4.imprint","IMPRINT",EDGE,{"derivedFrom":subQ1})]})});}
            var Q4;
            {var subQ0=sQuery(id+"F0.wireOp",EDGE,"E25.0");var subQ1=sQuery(id+"F0.wireOp",EDGE,"E25.1");var subQ2=sQuery(id+"F0.wireOp",EDGE,"E25.2");var subQ3=sQuery(id+"F0.wireOp",EDGE,"E25.3");var subQ4=sQuery(id+"F0.wireOp",EDGE,"E25.4");var subQ5=sQuery(id+"F0.wireOp",EDGE,"E25.5");var subQ6=sQuery(id+"F0.wireOp",EDGE,"E25.6");var subQ7=sQuery(id+"F0.wireOp",EDGE,"E25.7");Q4=makeQuery(id+"F8.boolean.opBoolean","INTERSECT",EDGE,{"derivedFrom":[makeQuery(id+"F5.boolean.opBoolean","SPLIT",FACE,{"disambiguationData":[TD([makeQuery(id+"F2.opExtrude","SWEPT_FACE",FACE,{"disambiguationData":[OSD([subQ0])]})])],"derivedFrom":makeQuery(id+"F3.boolean.opBoolean","COPY",FACE,{"derivedFrom":makeQuery(id+"F3.opExtrude","CAP_FACE",FACE,{"disambiguationData":[OSD([subQ0,subQ1,subQ2,subQ3,subQ4,subQ5,subQ6,subQ7])],"isStart":false})})}),makeQuery(id+"F8.opExtrude","SWEPT_FACE",FACE,{"disambiguationData":[OSD([sQuery(id+"F7.wireOp",EDGE,"E67")])]})]});}
            var Q5;
            Q5=makeQuery(id+"F8.boolean.opBoolean","INTERSECT",EDGE,{"disambiguationData":[OD(0.0)],"derivedFrom":[makeQuery(id+"F5.opExtrude","SWEPT_FACE",FACE,{"disambiguationData":[OSD([sQuery(id+"F4.wireOp",EDGE,"E30")])]}),makeQuery(id+"F8.opExtrude","SWEPT_FACE",FACE,{"disambiguationData":[OSD([sQuery(id+"F7.wireOp",EDGE,"E67")])]})]});
            fillet(context, id + "F14", {"entities" : qUnion([Q0, Q1, Q2, Q3, Q4, Q5]), "radius" : 3 * mm, "tangentPropagation" : true, "allowEdgeOverflow" : false});
        }
        {
            var Q0;
            Q0=makeQuery(id+"F1.opExtrude","CAP_EDGE",EDGE,{"disambiguationData":[OSD([sQuery(id+"F0.wireOp",EDGE,"E1.bottom")])],"isStart":false});
            fillet(context, id + "F15", {"entities" : qUnion([Q0]), "radius" : 2 * mm, "tangentPropagation" : true, "allowEdgeOverflow" : false});
        }
        {
            var Q0;
            {var subQ0=sQuery(id+"F0.wireOp",EDGE,"E21.filletArc");var subQ1=sQuery(id+"F0.wireOp",EDGE,"E7");var subQ2=sQuery(id+"F0.wireOp",EDGE,"E6");var subQ3=sQuery(id+"F0.wireOp",EDGE,"E5");var subQ4=sQuery(id+"F0.wireOp",EDGE,"E4");var subQ5=sQuery(id+"F0.wireOp",EDGE,"E22.filletArc");var subQ6=sQuery(id+"F0.wireOp",EDGE,"E1.bottom");var subQ7=sQuery(id+"F0.wireOp",EDGE,"E1.right");var subQ8=sQuery(id+"F0.wireOp",EDGE,"E1.top");var subQ9=sQuery(id+"F0.wireOp",EDGE,"E1.left");var subQ10=sQuery(id+"F0.wireOp",EDGE,"E23.filletArc");var subQ11=sQuery(id+"F0.wireOp",EDGE,"E24.filletArc");Q0=makeQuery(id+"F2.boolean.opBoolean","SPLIT",FACE,{"disambiguationData":[TD([makeQuery(id+"F1.opExtrude","SWEPT_FACE",FACE,{"disambiguationData":[OSD([subQ6])]})])],"derivedFrom":makeQuery(id+"F1.opExtrude","CAP_FACE",FACE,{"disambiguationData":[OSD([subQ6,subQ8,subQ9,subQ7,subQ4,subQ3,subQ2,subQ1,subQ0,subQ5,subQ10,subQ11])],"isStart":true})});}
            var sketch = newSketch(context, id + "F16", { "sketchPlane" : qUnion([Q0])});
            skLineSegment(sketch, "E79.0.0", {"start": v(80, 90) * mm, "end": v(33, 90) * mm});
            skArc(sketch, "E79.0.1", {"start": v(-80, 90) * mm, "mid": v(-87.07, 87.07) * mm, "end": v(-90, 80) * mm});
            skLineSegment(sketch, "E79.0.2", {"start": v(-90, 80) * mm, "end": v(-90, -80) * mm});
            skArc(sketch, "E79.0.3", {"start": v(-90, -80) * mm, "mid": v(-87.07, -87.07) * mm, "end": v(-80, -90) * mm});
            skLineSegment(sketch, "E79.0.4", {"start": v(-80, -90) * mm, "end": v(-33, -90) * mm});
            skArc(sketch, "E79.0.5", {"start": v(80, -90) * mm, "mid": v(87.07, -87.07) * mm, "end": v(90, -80) * mm});
            skLineSegment(sketch, "E79.0.6", {"start": v(90, -80) * mm, "end": v(90, 80) * mm});
            skArc(sketch, "E79.0.7", {"start": v(90, 80) * mm, "mid": v(87.07, 87.07) * mm, "end": v(80, 90) * mm});
            skCircle(sketch, "E80.0", {"center": v(-80, 80) * mm, "radius": 4 * mm});
            skCircle(sketch, "E81.0", {"center": v(80, 80) * mm, "radius": 4 * mm});
            skCircle(sketch, "E82.0", {"center": v(80, -80) * mm, "radius": 4 * mm});
            skCircle(sketch, "E83.0", {"center": v(-80, -80) * mm, "radius": 4 * mm});
            skArc(sketch, "E84.0", {"start": v(-77.08, -48.04) * mm, "mid": v(0, -80) * mm, "end": v(77.08, -48.04) * mm});
            skArc(sketch, "E85.0", {"start": v(-80, -40.98) * mm, "mid": v(-79.24, -44.8) * mm, "end": v(-77.08, -48.04) * mm});
            skLineSegment(sketch, "E86.0", {"start": v(-80, 40.98) * mm, "end": v(-80, -40.98) * mm});
            skArc(sketch, "E87.0", {"start": v(-77.08, 48.04) * mm, "mid": v(-79.24, 44.8) * mm, "end": v(-80, 40.98) * mm});
            skArc(sketch, "E88.0", {"start": v(77.08, 48.04) * mm, "mid": v(0, 80) * mm, "end": v(-77.08, 48.04) * mm});
            skArc(sketch, "E89.0", {"start": v(80, 40.98) * mm, "mid": v(79.24, 44.8) * mm, "end": v(77.08, 48.04) * mm});
            skLineSegment(sketch, "E90.0", {"start": v(80, 40.98) * mm, "end": v(80, -40.98) * mm});
            skLineSegment(sketch, "E91", {"start": v(0, 90) * mm, "end": v(0, 120) * mm, "construction": true});
            skCircle(sketch, "E92", {"center": v(0, 120) * mm, "radius": 6 * mm});
            skLineSegment(sketch, "E93", {"start": v(-33, 90) * mm, "end": v(-15, 108) * mm});
            skLineSegment(sketch, "E94", {"start": v(-15, 108) * mm, "end": v(-15, 120) * mm});
            skLineSegment(sketch, "E95", {"start": v(15, 120) * mm, "end": v(15, 108) * mm});
            skLineSegment(sketch, "E96", {"start": v(15, 108) * mm, "end": v(33, 90) * mm});
            skArc(sketch, "E97", {"start": v(15, 120) * mm, "mid": v(0, 135) * mm, "end": v(-15, 120) * mm});
            skLineSegment(sketch, "E98", {"start": v(-90, 0) * mm, "end": v(90, 0) * mm, "construction": true});
            skLineSegment(sketch, "E99.MirrorCS", {"start": v(-33, -90) * mm, "end": v(-15, -108) * mm});
            skLineSegment(sketch, "E100.MirrorCS", {"start": v(-15, -108) * mm, "end": v(-15, -120) * mm});
            skArc(sketch, "E101.MirrorCS", {"start": v(15, -120) * mm, "mid": v(0, -135) * mm, "end": v(-15, -120) * mm});
            skLineSegment(sketch, "E102.MirrorCS", {"start": v(15, -120) * mm, "end": v(15, -108) * mm});
            skLineSegment(sketch, "E103.MirrorCS", {"start": v(15, -108) * mm, "end": v(33, -90) * mm});
            skCircle(sketch, "E104.MirrorC", {"center": v(0, -120) * mm, "radius": 6 * mm});
            skLineSegment(sketch, "E105.MirrorCS", {"start": v(0, -90) * mm, "end": v(0, -120) * mm, "construction": true});
            skLineSegment(sketch, "E106.trimOffspring", {"start": v(-33, 90) * mm, "end": v(-80, 90) * mm});
            skLineSegment(sketch, "E107.trimOffspring", {"start": v(33, -90) * mm, "end": v(80, -90) * mm});
            skArc(sketch, "E108.0", {"start": v(77.08, -48.04) * mm, "mid": v(79.24, -44.8) * mm, "end": v(80, -40.98) * mm});
            skSolve(sketch);
        }
        {
            var Q0;
            Q0 = qSketchRegion(id + "F16", true);
            var Q1;
            Q1=makeQuery(id+"F2.opExtrude","CAP_FACE",FACE,{"disambiguationData":[OSD([sQuery(id+"F0.wireOp",EDGE,"E12"),sQuery(id+"F0.wireOp",EDGE,"E13"),sQuery(id+"F0.wireOp",EDGE,"E14"),sQuery(id+"F0.wireOp",EDGE,"E15"),sQuery(id+"F0.wireOp",EDGE,"E17.filletArc"),sQuery(id+"F0.wireOp",EDGE,"E18.filletArc"),sQuery(id+"F0.wireOp",EDGE,"E19.filletArc"),sQuery(id+"F0.wireOp",EDGE,"E20.filletArc"),sQuery(id+"F0.wireOp",EDGE,"E25.0"),sQuery(id+"F0.wireOp",EDGE,"E25.1"),sQuery(id+"F0.wireOp",EDGE,"E25.2"),sQuery(id+"F0.wireOp",EDGE,"E25.3"),sQuery(id+"F0.wireOp",EDGE,"E25.4"),sQuery(id+"F0.wireOp",EDGE,"E25.5"),sQuery(id+"F0.wireOp",EDGE,"E25.6"),sQuery(id+"F0.wireOp",EDGE,"E25.7")])],"isStart":false});
            extrude(context, id + "F17", {"entities" : qUnion([Q0]), "endBound" : BoundingType.UP_TO_SURFACE, "endBoundEntityFace" : qUnion([Q1]), "depth" : 25 * mm});
        }
    });
